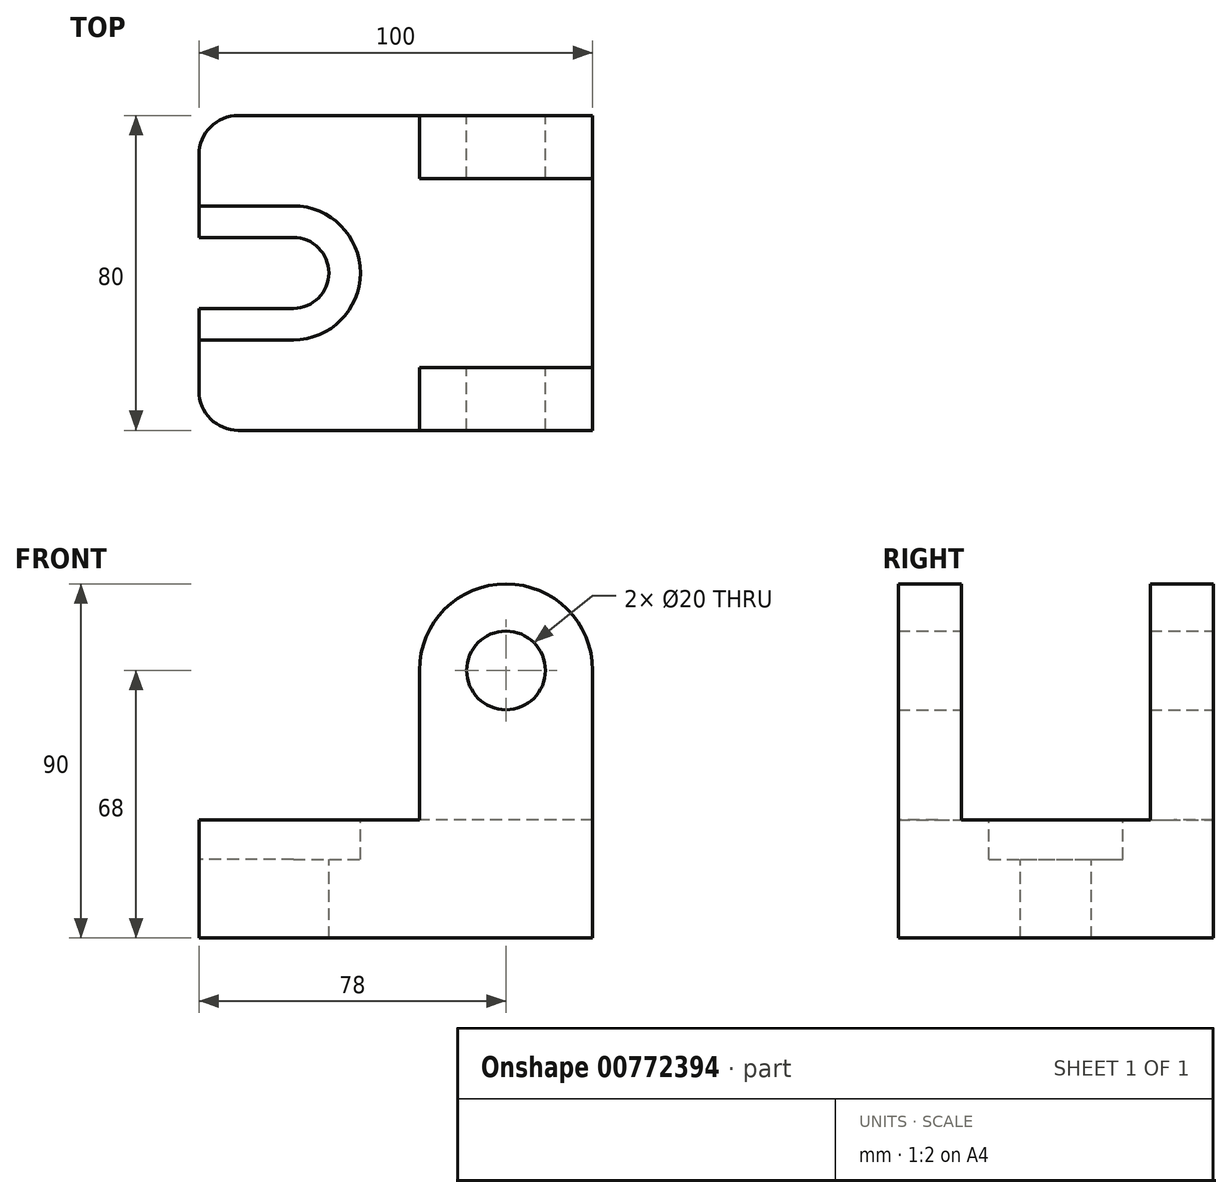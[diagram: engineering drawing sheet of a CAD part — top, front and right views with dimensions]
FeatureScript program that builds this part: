
annotation { "Feature Type Name" : "Feature", "Feature Type Description" : "" }
export const myFeature = defineFeature(function(context is Context, id is Id, definition is map)
    precondition{}
    {
        {
            var Q0;
            Q0=qCreatedBy(makeId("Front.planeOp"),FACE);
            var sketch = newSketch(context, id + "F0", { "sketchPlane" : qUnion([Q0])});
            skLineSegment(sketch, "E0.bottom", {"start": v(0, 0) * mm, "end": v(100, 0) * mm});
            skLineSegment(sketch, "E0.top", {"start": v(0, 30) * mm, "end": v(56, 30) * mm});
            skLineSegment(sketch, "E0.left", {"start": v(0, 0) * mm, "end": v(0, 30) * mm});
            skLineSegment(sketch, "E0.right", {"start": v(100, 0) * mm, "end": v(100, 30) * mm});
            skLineSegment(sketch, "E1.bottom", {"start": v(100, 30) * mm, "end": v(56, 30) * mm});
            skLineSegment(sketch, "E1.left", {"start": v(100, 30) * mm, "end": v(100, 68) * mm});
            skLineSegment(sketch, "E1.right", {"start": v(56, 30) * mm, "end": v(56, 68) * mm});
            skArc(sketch, "E2", {"start": v(100, 68) * mm, "mid": v(78, 90) * mm, "end": v(56, 68) * mm});
            skCircle(sketch, "E3", {"center": v(78, 68) * mm, "radius": 10 * mm});
            skSolve(sketch);
        }
        {
            var Q0;
            Q0=makeQuery(id+"F0.imprint","IMPRINT",FACE,{"disambiguationData":[TD([[makeQuery(id+"F0.imprint","IMPRINT",EDGE,{"derivedFrom":sQuery(id+"F0.wireOp",EDGE,"E0.bottom")}),1.0]])]});
            var Q1;
            Q1=makeQuery(id+"F0.imprint","IMPRINT",FACE,{"disambiguationData":[TD([[makeQuery(id+"F0.imprint","IMPRINT",EDGE,{"derivedFrom":sQuery(id+"F0.wireOp",EDGE,"E1.bottom")}),-1.0]])]});
            extrude(context, id + "F1", {"entities" : qUnion([Q0, Q1]), "endBound" : BoundingType.SYMMETRIC, "depth" : 80 * mm, "offsetDistance" : 25 * mm});
        }
        {
            var Q0;
            Q0=makeQuery(id+"F0.imprint","IMPRINT",FACE,{"disambiguationData":[TD([[makeQuery(id+"F0.imprint","IMPRINT",EDGE,{"derivedFrom":sQuery(id+"F0.wireOp",EDGE,"E1.bottom")}),-1.0]])]});
            extrude(context, id + "F2", {"entities" : qUnion([Q0]), "operationType" : NewBodyOperationType.REMOVE, "endBound" : BoundingType.SYMMETRIC, "oppositeDirection" : true, "depth" : 48 * mm, "offsetDistance" : 25 * mm});
        }
        {
            var Q0;
            Q0=makeQuery(id+"F2.boolean.opBoolean","MERGE",FACE,{"derivedFrom":[makeQuery(id+"F1.opExtrude","SWEPT_FACE",FACE,{"disambiguationData":[OSD([sQuery(id+"F0.wireOp",EDGE,"E0.top")])]}),makeQuery(id+"F2.opExtrude","SWEPT_FACE",FACE,{"disambiguationData":[OSD([sQuery(id+"F0.wireOp",EDGE,"E1.bottom")])]})]});
            var sketch = newSketch(context, id + "F3", { "sketchPlane" : qUnion([Q0])});
            skLineSegment(sketch, "E4", {"start": v(0, 0) * mm, "end": v(24, 0) * mm, "construction": true});
            skArc(sketch, "E5", {"start": v(24, 17) * mm, "mid": v(41, 0) * mm, "end": v(24, -17) * mm});
            skLineSegment(sketch, "E6", {"start": v(24, -17) * mm, "end": v(0, -17) * mm});
            skLineSegment(sketch, "E7", {"start": v(24, 17) * mm, "end": v(0, 17) * mm});
            skLineSegment(sketch, "E8.0", {"start": v(24, 9) * mm, "end": v(0, 9) * mm});
            skArc(sketch, "E8.1", {"start": v(24, 9) * mm, "mid": v(33, 0) * mm, "end": v(24, -9) * mm});
            skLineSegment(sketch, "E8.2", {"start": v(24, -9) * mm, "end": v(0, -9) * mm});
            skSolve(sketch);
        }
        {
            var Q0;
            Q0=makeQuery(id+"F2.boolean.opBoolean","MERGE",FACE,{"derivedFrom":[makeQuery(id+"F1.opExtrude","SWEPT_FACE",FACE,{"disambiguationData":[OSD([sQuery(id+"F0.wireOp",EDGE,"E0.top")])]}),makeQuery(id+"F2.opExtrude","SWEPT_FACE",FACE,{"disambiguationData":[OSD([sQuery(id+"F0.wireOp",EDGE,"E1.bottom")])]})]});
            var sketch = newSketch(context, id + "F4", { "sketchPlane" : qUnion([Q0])});
            skLineSegment(sketch, "E9", {"start": v(0, 0) * mm, "end": v(24, 0) * mm, "construction": true});
            skArc(sketch, "E10", {"start": v(24, -17) * mm, "mid": v(41, 0) * mm, "end": v(24, 17) * mm});
            skLineSegment(sketch, "E11", {"start": v(24, -17) * mm, "end": v(0, -17) * mm});
            skLineSegment(sketch, "E12", {"start": v(24, 17) * mm, "end": v(0, 17) * mm});
            skLineSegment(sketch, "E13", {"start": v(24, -17) * mm, "end": v(24, 0) * mm, "construction": true});
            skLineSegment(sketch, "E14", {"start": v(24, 17) * mm, "end": v(24, 0) * mm, "construction": true});
            skLineSegment(sketch, "E15", {"start": v(0, 17) * mm, "end": v(0, -17) * mm});
            skLineSegment(sketch, "E16.0", {"start": v(24, -9) * mm, "end": v(0, -9) * mm});
            skArc(sketch, "E16.1", {"start": v(24, -9) * mm, "mid": v(33, 0) * mm, "end": v(24, 9) * mm});
            skLineSegment(sketch, "E16.2", {"start": v(24, 9) * mm, "end": v(0, 9) * mm});
            skSolve(sketch);
        }
        {
            var Q0;
            Q0=qSketchRegion(id+"F4",true);
            extrude(context, id + "F5", {"entities" : qUnion([Q0]), "operationType" : NewBodyOperationType.REMOVE, "oppositeDirection" : true, "depth" : 10 * mm, "offsetDistance" : 25 * mm});
        }
        {
            var Q0;
            {var subQ0=sQuery(id+"F4.wireOp",EDGE,"E16.0");Q0=makeQuery(id+"F4.imprint","IMPRINT",FACE,{"disambiguationData":[TD([[makeQuery(id+"F4.imprint","IMPRINT",EDGE,{"derivedFrom":subQ0}),-1.0]])]});}
            extrude(context, id + "F6", {"entities" : qUnion([Q0]), "operationType" : NewBodyOperationType.REMOVE, "endBound" : BoundingType.THROUGH_ALL, "oppositeDirection" : true, "depth" : 25 * mm, "offsetDistance" : 25 * mm});
        }
        {
            var Q0;
            Q0=makeQuery(id+"F1.opExtrude","CAP_EDGE",EDGE,{"disambiguationData":[OSD([sQuery(id+"F0.wireOp",EDGE,"E0.left")])],"isStart":false});
            var Q1;
            Q1=makeQuery(id+"F1.opExtrude","CAP_EDGE",EDGE,{"disambiguationData":[OSD([sQuery(id+"F0.wireOp",EDGE,"E0.left")])],"isStart":true});
            fillet(context, id + "F7", {"entities" : qUnion([Q0, Q1]), "radius" : 10 * mm, "tangentPropagation" : true, "allowEdgeOverflow" : false});
        }
    });
